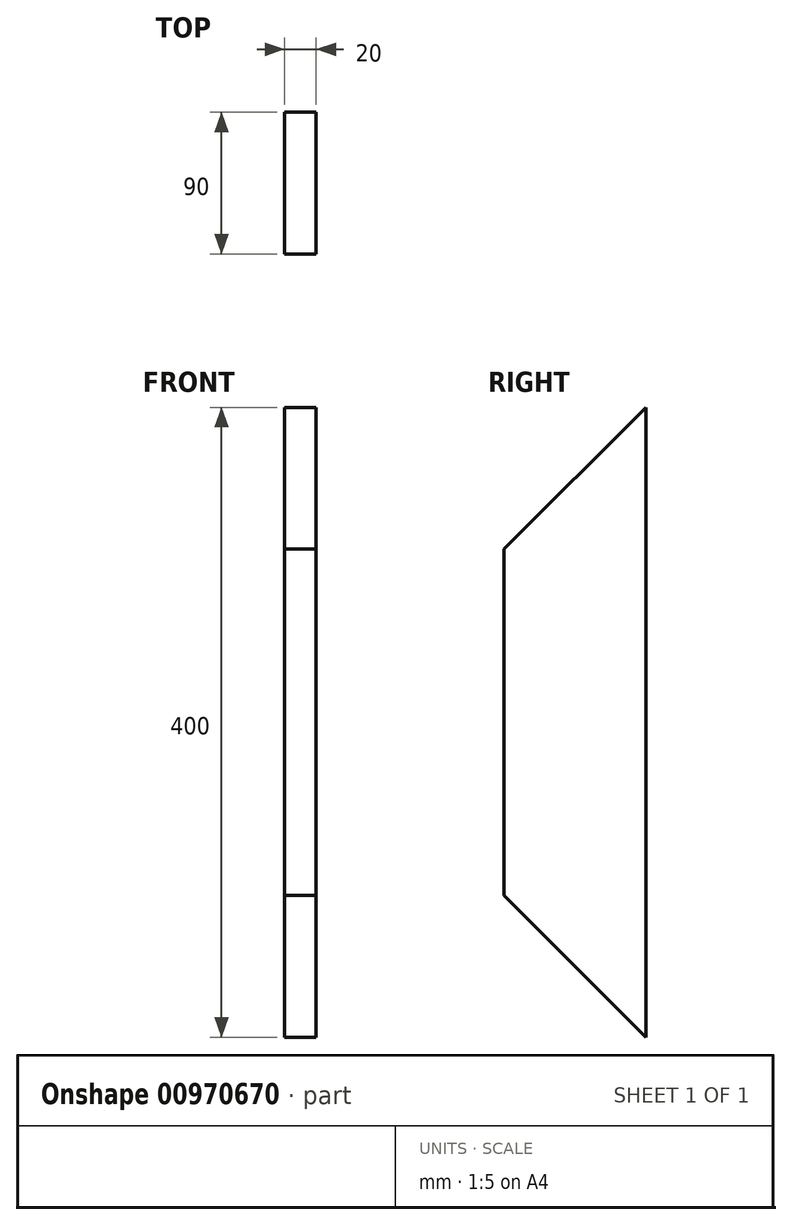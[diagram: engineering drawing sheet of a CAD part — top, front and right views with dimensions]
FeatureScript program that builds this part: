
annotation { "Feature Type Name" : "Feature", "Feature Type Description" : "" }
export const myFeature = defineFeature(function(context is Context, id is Id, definition is map)
    precondition{}
    {
        {
            var Q0;
            Q0=qCreatedBy(makeId("Top.planeOp"),FACE);
            var sketch = newSketch(context, id + "F0", { "sketchPlane" : qUnion([Q0])});
            skLineSegment(sketch, "E0.bottom", {"start": v(-20.98, 60.27) * mm, "end": v(-0.98, 60.27) * mm});
            skLineSegment(sketch, "E0.top", {"start": v(-20.98, -29.73) * mm, "end": v(-0.98, -29.73) * mm});
            skLineSegment(sketch, "E0.left", {"start": v(-20.98, 60.27) * mm, "end": v(-20.98, -29.73) * mm});
            skLineSegment(sketch, "E0.right", {"start": v(-0.98, 60.27) * mm, "end": v(-0.98, -29.73) * mm});
            skSolve(sketch);
        }
        {
            var Q0;
            Q0 = qSketchRegion(id + "F0", true);
            extrude(context, id + "F1", {"entities" : qUnion([Q0]), "depth" : 400 * mm, "offsetDistance" : 25 * mm});
        }
        {
            var Q0;
            Q0=makeQuery(id+"F1.opExtrude","SWEPT_FACE",FACE,{"disambiguationData":[OSD([sQuery(id+"F0.wireOp",EDGE,"E0.right")])]});
            var sketch = newSketch(context, id + "F2", { "sketchPlane" : qUnion([Q0])});
            skLineSegment(sketch, "E1", {"start": v(60.27, 400) * mm, "end": v(-29.73, 310) * mm});
            skLineSegment(sketch, "E2", {"start": v(60.27, 0) * mm, "end": v(-29.73, 90) * mm});
            skLineSegment(sketch, "E3.0", {"start": v(60.27, 0) * mm, "end": v(-29.73, 0) * mm});
            skLineSegment(sketch, "E4.0", {"start": v(-29.73, 400) * mm, "end": v(-29.73, 0) * mm});
            skLineSegment(sketch, "E5.0", {"start": v(60.27, 400) * mm, "end": v(-29.73, 400) * mm});
            skSolve(sketch);
        }
        {
            var Q0;
            Q0 = qSketchRegion(id + "F2", true);
            extrude(context, id + "F3", {"entities" : qUnion([Q0]), "operationType" : NewBodyOperationType.REMOVE, "endBound" : BoundingType.THROUGH_ALL, "oppositeDirection" : true, "depth" : 25 * mm, "offsetDistance" : 25 * mm});
        }
    });
